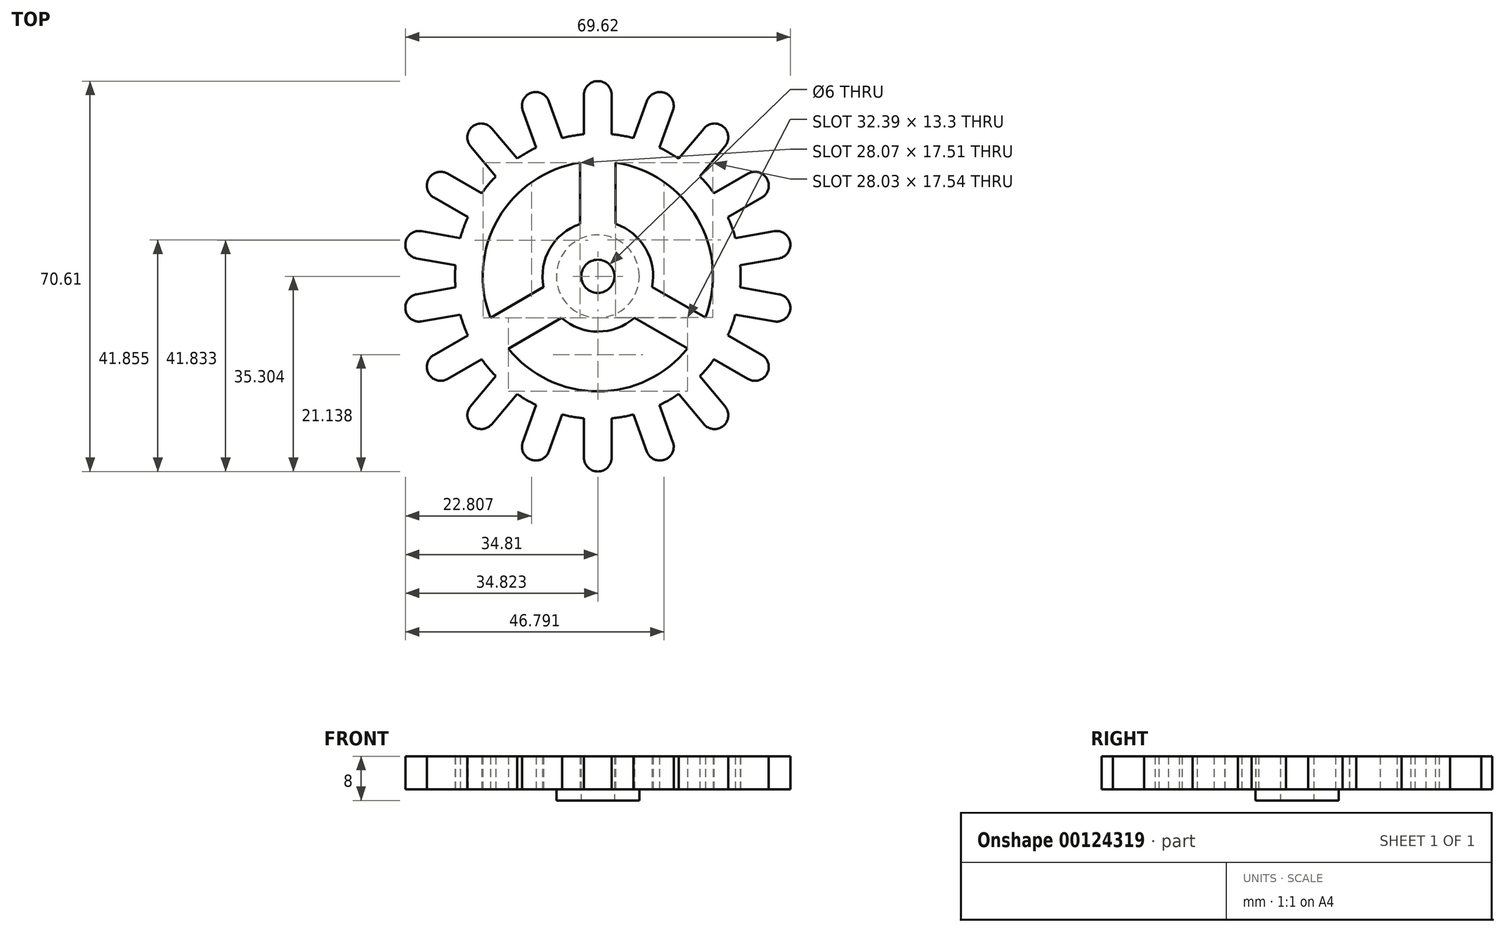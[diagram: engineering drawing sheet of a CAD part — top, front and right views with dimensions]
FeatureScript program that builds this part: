
annotation { "Feature Type Name" : "Feature", "Feature Type Description" : "" }
export const myFeature = defineFeature(function(context is Context, id is Id, definition is map)
    precondition{}
    {
        {
            var Q0;
            Q0=qCreatedBy(makeId("Top.planeOp"),FACE);
            var sketch = newSketch(context, id + "F0", { "sketchPlane" : qUnion([Q0])});
            skLineSegment(sketch, "E0.top", {"start": v(-2.5, 0) * mm, "end": v(2.5, 0) * mm});
            skLineSegment(sketch, "E0.left", {"start": v(-2.5, 7.1) * mm, "end": v(-2.5, 0) * mm});
            skLineSegment(sketch, "E0.right", {"start": v(2.5, 7.1) * mm, "end": v(2.5, 0) * mm});
            skPoint(sketch, "E1.visualSharp", {"position": v(-2.5, 10) * mm});
            skArc(sketch, "E1.filletArc", {"start": v(0, 9.6) * mm, "mid": v(-1.77, 8.88) * mm, "end": v(-2.5, 7.1) * mm});
            skPoint(sketch, "E2.visualSharp", {"position": v(2.5, 10) * mm});
            skArc(sketch, "E2.filletArc", {"start": v(2.5, 7.1) * mm, "mid": v(1.77, 8.88) * mm, "end": v(0, 9.6) * mm});
            skArc(sketch, "E3.1.0", {"start": v(-12.08, 7.48) * mm, "mid": v(-13.49, 6.19) * mm, "end": v(-13.57, 4.28) * mm});
            skArc(sketch, "E3.1.1", {"start": v(-8.87, 5.99) * mm, "mid": v(-10.16, 7.4) * mm, "end": v(-12.08, 7.48) * mm});
            skLineSegment(sketch, "E3.1.2", {"start": v(-8.87, 5.99) * mm, "end": v(-6.44, -0.7) * mm});
            skLineSegment(sketch, "E3.1.3", {"start": v(-11.14, -2.4) * mm, "end": v(-6.44, -0.7) * mm});
            skLineSegment(sketch, "E3.1.4", {"start": v(-13.57, 4.28) * mm, "end": v(-11.14, -2.4) * mm});
            skArc(sketch, "E3.2.0", {"start": v(-22.7, 1.35) * mm, "mid": v(-23.58, -0.35) * mm, "end": v(-23, -2.17) * mm});
            skArc(sketch, "E3.2.1", {"start": v(-19.17, 1.04) * mm, "mid": v(-20.87, 1.93) * mm, "end": v(-22.7, 1.35) * mm});
            skLineSegment(sketch, "E3.2.2", {"start": v(-19.17, 1.04) * mm, "end": v(-14.6, -4.4) * mm});
            skLineSegment(sketch, "E3.2.3", {"start": v(-18.43, -7.62) * mm, "end": v(-14.6, -4.4) * mm});
            skLineSegment(sketch, "E3.2.4", {"start": v(-23, -2.17) * mm, "end": v(-18.43, -7.62) * mm});
            skPoint(sketch, "E3.center", {"position": v(0, -25.7) * mm});
            skArc(sketch, "E4.3.3.0", {"start": v(-30.58, -8.04) * mm, "mid": v(-30.82, -9.94) * mm, "end": v(-29.66, -11.46) * mm});
            skArc(sketch, "E4.4.3.0", {"start": v(-27.16, -7.13) * mm, "mid": v(-29.06, -6.88) * mm, "end": v(-30.58, -8.04) * mm});
            skLineSegment(sketch, "E4.8.3.0", {"start": v(-27.16, -7.13) * mm, "end": v(-21, -10.68) * mm});
            skLineSegment(sketch, "E4.11.3.0", {"start": v(-23.5, -15.01) * mm, "end": v(-21, -10.68) * mm});
            skLineSegment(sketch, "E4.14.3.0", {"start": v(-29.66, -11.46) * mm, "end": v(-23.5, -15.01) * mm});
            skArc(sketch, "E5.3.4.0", {"start": v(-34.77, -19.57) * mm, "mid": v(-34.35, -21.43) * mm, "end": v(-32.74, -22.46) * mm});
            skArc(sketch, "E5.4.4.0", {"start": v(-31.87, -17.54) * mm, "mid": v(-33.74, -17.95) * mm, "end": v(-34.77, -19.57) * mm});
            skLineSegment(sketch, "E5.8.4.0", {"start": v(-31.87, -17.54) * mm, "end": v(-24.87, -18.77) * mm});
            skLineSegment(sketch, "E5.11.4.0", {"start": v(-25.74, -23.7) * mm, "end": v(-24.87, -18.77) * mm});
            skLineSegment(sketch, "E5.14.4.0", {"start": v(-32.74, -22.46) * mm, "end": v(-25.74, -23.7) * mm});
            skArc(sketch, "E6.3.5.0", {"start": v(-34.77, -31.83) * mm, "mid": v(-33.74, -33.44) * mm, "end": v(-31.87, -33.85) * mm});
            skArc(sketch, "E6.4.5.0", {"start": v(-32.74, -28.93) * mm, "mid": v(-34.35, -29.96) * mm, "end": v(-34.77, -31.83) * mm});
            skLineSegment(sketch, "E6.8.5.0", {"start": v(-32.74, -28.93) * mm, "end": v(-25.74, -27.7) * mm});
            skLineSegment(sketch, "E6.11.5.0", {"start": v(-24.87, -32.62) * mm, "end": v(-25.74, -27.7) * mm});
            skLineSegment(sketch, "E6.14.5.0", {"start": v(-31.87, -33.85) * mm, "end": v(-24.87, -32.62) * mm});
            skArc(sketch, "E7.3.6.0", {"start": v(-30.58, -43.35) * mm, "mid": v(-29.06, -44.51) * mm, "end": v(-27.16, -44.26) * mm});
            skArc(sketch, "E7.4.6.0", {"start": v(-29.66, -39.93) * mm, "mid": v(-30.82, -41.45) * mm, "end": v(-30.58, -43.35) * mm});
            skLineSegment(sketch, "E7.8.6.0", {"start": v(-29.66, -39.93) * mm, "end": v(-23.5, -36.38) * mm});
            skLineSegment(sketch, "E7.11.6.0", {"start": v(-21, -40.7) * mm, "end": v(-23.5, -36.38) * mm});
            skLineSegment(sketch, "E7.14.6.0", {"start": v(-27.16, -44.26) * mm, "end": v(-21, -40.7) * mm});
            skArc(sketch, "E8.3.7.0", {"start": v(-22.7, -52.74) * mm, "mid": v(-20.87, -53.32) * mm, "end": v(-19.17, -52.43) * mm});
            skArc(sketch, "E8.4.7.0", {"start": v(-23, -49.22) * mm, "mid": v(-23.58, -51.04) * mm, "end": v(-22.7, -52.74) * mm});
            skLineSegment(sketch, "E8.8.7.0", {"start": v(-23, -49.22) * mm, "end": v(-18.43, -43.77) * mm});
            skLineSegment(sketch, "E8.11.7.0", {"start": v(-14.6, -46.99) * mm, "end": v(-18.43, -43.77) * mm});
            skLineSegment(sketch, "E8.14.7.0", {"start": v(-19.17, -52.43) * mm, "end": v(-14.6, -46.99) * mm});
            skArc(sketch, "E9.3.8.0", {"start": v(-12.08, -58.87) * mm, "mid": v(-10.16, -58.79) * mm, "end": v(-8.87, -57.38) * mm});
            skArc(sketch, "E9.4.8.0", {"start": v(-13.57, -55.67) * mm, "mid": v(-13.49, -57.58) * mm, "end": v(-12.08, -58.87) * mm});
            skLineSegment(sketch, "E9.8.8.0", {"start": v(-13.57, -55.67) * mm, "end": v(-11.14, -48.99) * mm});
            skLineSegment(sketch, "E9.11.8.0", {"start": v(-6.44, -50.7) * mm, "end": v(-11.14, -48.99) * mm});
            skLineSegment(sketch, "E9.14.8.0", {"start": v(-8.87, -57.38) * mm, "end": v(-6.44, -50.7) * mm});
            skArc(sketch, "E10.3.9.0", {"start": v(0, -61) * mm, "mid": v(1.77, -60.27) * mm, "end": v(2.5, -58.5) * mm});
            skArc(sketch, "E10.4.9.0", {"start": v(-2.5, -58.5) * mm, "mid": v(-1.77, -60.27) * mm, "end": v(0, -61) * mm});
            skLineSegment(sketch, "E10.8.9.0", {"start": v(-2.5, -58.5) * mm, "end": v(-2.5, -51.4) * mm});
            skLineSegment(sketch, "E10.11.9.0", {"start": v(2.5, -51.4) * mm, "end": v(-2.5, -51.4) * mm});
            skLineSegment(sketch, "E10.14.9.0", {"start": v(2.5, -58.5) * mm, "end": v(2.5, -51.4) * mm});
            skArc(sketch, "E11.3.10.0", {"start": v(12.08, -58.87) * mm, "mid": v(13.49, -57.58) * mm, "end": v(13.57, -55.67) * mm});
            skArc(sketch, "E11.4.10.0", {"start": v(8.87, -57.38) * mm, "mid": v(10.16, -58.79) * mm, "end": v(12.08, -58.87) * mm});
            skLineSegment(sketch, "E11.8.10.0", {"start": v(8.87, -57.38) * mm, "end": v(6.44, -50.7) * mm});
            skLineSegment(sketch, "E11.11.10.0", {"start": v(11.14, -48.99) * mm, "end": v(6.44, -50.7) * mm});
            skLineSegment(sketch, "E11.14.10.0", {"start": v(13.57, -55.67) * mm, "end": v(11.14, -48.99) * mm});
            skArc(sketch, "E12.3.11.0", {"start": v(22.7, -52.74) * mm, "mid": v(23.58, -51.04) * mm, "end": v(23, -49.22) * mm});
            skArc(sketch, "E12.4.11.0", {"start": v(19.17, -52.43) * mm, "mid": v(20.87, -53.32) * mm, "end": v(22.7, -52.74) * mm});
            skLineSegment(sketch, "E12.8.11.0", {"start": v(19.17, -52.43) * mm, "end": v(14.6, -46.99) * mm});
            skLineSegment(sketch, "E12.11.11.0", {"start": v(18.43, -43.77) * mm, "end": v(14.6, -46.99) * mm});
            skLineSegment(sketch, "E12.14.11.0", {"start": v(23, -49.22) * mm, "end": v(18.43, -43.77) * mm});
            skCircle(sketch, "E13", {"center": v(0, -25.7) * mm, "radius": 25.82 * mm});
            skCircle(sketch, "E14", {"center": v(0, -25.7) * mm, "radius": 20.82 * mm});
            skArc(sketch, "E15.3.12.0", {"start": v(30.58, -43.35) * mm, "mid": v(30.82, -41.45) * mm, "end": v(29.66, -39.93) * mm});
            skArc(sketch, "E15.4.12.0", {"start": v(27.16, -44.26) * mm, "mid": v(29.06, -44.51) * mm, "end": v(30.58, -43.35) * mm});
            skLineSegment(sketch, "E15.8.12.0", {"start": v(27.16, -44.26) * mm, "end": v(21, -40.7) * mm});
            skLineSegment(sketch, "E15.11.12.0", {"start": v(23.5, -36.38) * mm, "end": v(21, -40.7) * mm});
            skLineSegment(sketch, "E15.14.12.0", {"start": v(29.66, -39.93) * mm, "end": v(23.5, -36.38) * mm});
            skArc(sketch, "E15.3.13.0", {"start": v(34.77, -31.83) * mm, "mid": v(34.35, -29.96) * mm, "end": v(32.74, -28.93) * mm});
            skArc(sketch, "E15.4.13.0", {"start": v(31.87, -33.85) * mm, "mid": v(33.74, -33.44) * mm, "end": v(34.77, -31.83) * mm});
            skLineSegment(sketch, "E15.8.13.0", {"start": v(31.87, -33.85) * mm, "end": v(24.87, -32.62) * mm});
            skLineSegment(sketch, "E15.11.13.0", {"start": v(25.74, -27.7) * mm, "end": v(24.87, -32.62) * mm});
            skLineSegment(sketch, "E15.14.13.0", {"start": v(32.74, -28.93) * mm, "end": v(25.74, -27.7) * mm});
            skArc(sketch, "E15.3.14.0", {"start": v(34.77, -19.57) * mm, "mid": v(33.74, -17.95) * mm, "end": v(31.87, -17.54) * mm});
            skArc(sketch, "E15.4.14.0", {"start": v(32.74, -22.46) * mm, "mid": v(34.35, -21.43) * mm, "end": v(34.77, -19.57) * mm});
            skLineSegment(sketch, "E15.8.14.0", {"start": v(32.74, -22.46) * mm, "end": v(25.74, -23.7) * mm});
            skLineSegment(sketch, "E15.11.14.0", {"start": v(24.87, -18.77) * mm, "end": v(25.74, -23.7) * mm});
            skLineSegment(sketch, "E15.14.14.0", {"start": v(31.87, -17.54) * mm, "end": v(24.87, -18.77) * mm});
            skArc(sketch, "E15.3.15.0", {"start": v(30.58, -8.04) * mm, "mid": v(29.06, -6.88) * mm, "end": v(27.16, -7.13) * mm});
            skArc(sketch, "E15.4.15.0", {"start": v(29.66, -11.46) * mm, "mid": v(30.82, -9.94) * mm, "end": v(30.58, -8.04) * mm});
            skLineSegment(sketch, "E15.8.15.0", {"start": v(29.66, -11.46) * mm, "end": v(23.5, -15.01) * mm});
            skLineSegment(sketch, "E15.11.15.0", {"start": v(21, -10.68) * mm, "end": v(23.5, -15.01) * mm});
            skLineSegment(sketch, "E15.14.15.0", {"start": v(27.16, -7.13) * mm, "end": v(21, -10.68) * mm});
            skArc(sketch, "E16.3.16.0", {"start": v(22.7, 1.35) * mm, "mid": v(20.87, 1.93) * mm, "end": v(19.17, 1.04) * mm});
            skArc(sketch, "E16.4.16.0", {"start": v(23, -2.17) * mm, "mid": v(23.58, -0.35) * mm, "end": v(22.7, 1.35) * mm});
            skLineSegment(sketch, "E16.8.16.0", {"start": v(23, -2.17) * mm, "end": v(18.43, -7.62) * mm});
            skLineSegment(sketch, "E16.11.16.0", {"start": v(14.6, -4.4) * mm, "end": v(18.43, -7.62) * mm});
            skLineSegment(sketch, "E16.14.16.0", {"start": v(19.17, 1.04) * mm, "end": v(14.6, -4.4) * mm});
            skArc(sketch, "E16.3.17.0", {"start": v(12.08, 7.48) * mm, "mid": v(10.16, 7.4) * mm, "end": v(8.87, 5.99) * mm});
            skArc(sketch, "E16.4.17.0", {"start": v(13.57, 4.28) * mm, "mid": v(13.49, 6.19) * mm, "end": v(12.08, 7.48) * mm});
            skLineSegment(sketch, "E16.8.17.0", {"start": v(13.57, 4.28) * mm, "end": v(11.14, -2.4) * mm});
            skLineSegment(sketch, "E16.11.17.0", {"start": v(6.44, -0.7) * mm, "end": v(11.14, -2.4) * mm});
            skLineSegment(sketch, "E16.14.17.0", {"start": v(8.87, 5.99) * mm, "end": v(6.44, -0.7) * mm});
            skCircle(sketch, "E17", {"center": v(0, -25.7) * mm, "radius": 10 * mm});
            skCircle(sketch, "E18", {"center": v(0, -25.7) * mm, "radius": 3 * mm});
            skCircle(sketch, "E19", {"center": v(0, -25.7) * mm, "radius": 7.5 * mm});
            skLineSegment(sketch, "E20.left", {"start": v(-3.25, -5.13) * mm, "end": v(-3.25, -16.24) * mm});
            skLineSegment(sketch, "E20.right", {"start": v(3.2, -5.13) * mm, "end": v(3.2, -16.22) * mm});
            skPoint(sketch, "E21", {"position": v(0, -4.88) * mm});
            skLineSegment(sketch, "E22.1.0", {"start": v(-16.18, -38.8) * mm, "end": v(-6.56, -33.24) * mm});
            skLineSegment(sketch, "E22.1.1", {"start": v(-19.42, -33.2) * mm, "end": v(-9.8, -27.65) * mm});
            skLineSegment(sketch, "E22.2.0", {"start": v(19.43, -33.16) * mm, "end": v(9.82, -27.6) * mm});
            skLineSegment(sketch, "E22.2.1", {"start": v(16.2, -38.76) * mm, "end": v(6.6, -33.21) * mm});
            skPoint(sketch, "E23", {"position": v(0, 9.6) * mm});
            skSolve(sketch);
        }
        {
            var Q0;
            {var subQ0=sQuery(id+"F0.wireOp",EDGE,"E6.11.5.0");Q0=makeQuery(id+"F0.imprint","IMPRINT",FACE,{"disambiguationData":[TD([[makeQuery(id+"F0.imprint","IMPRINT",EDGE,{"derivedFrom":subQ0}),1.0]])]});}
            var Q1;
            {var subQ0=sQuery(id+"F0.wireOp",EDGE,"E22.1.0");Q1=makeQuery(id+"F0.imprint","IMPRINT",FACE,{"disambiguationData":[TD([[makeQuery(id+"F0.imprint","IMPRINT",EDGE,{"derivedFrom":subQ0}),1.0]])]});}
            var Q2;
            Q2=makeQuery(id+"F0.imprint","IMPRINT",FACE,{"disambiguationData":[TD([[makeQuery(id+"F0.imprint","IMPRINT",EDGE,{"derivedFrom":sQuery(id+"F0.wireOp",EDGE,"E15.3.14.0")}),1.0]])]});
            var Q3;
            Q3=makeQuery(id+"F0.imprint","IMPRINT",FACE,{"disambiguationData":[TD([[makeQuery(id+"F0.imprint","IMPRINT",EDGE,{"derivedFrom":sQuery(id+"F0.wireOp",EDGE,"E12.3.11.0")}),1.0]])]});
            var Q4;
            Q4=makeQuery(id+"F0.imprint","IMPRINT",FACE,{"disambiguationData":[TD([[makeQuery(id+"F0.imprint","IMPRINT",EDGE,{"derivedFrom":sQuery(id+"F0.wireOp",EDGE,"E11.3.10.0")}),1.0]])]});
            var Q5;
            Q5=makeQuery(id+"F0.imprint","IMPRINT",FACE,{"disambiguationData":[TD([[makeQuery(id+"F0.imprint","IMPRINT",EDGE,{"derivedFrom":sQuery(id+"F0.wireOp",EDGE,"E10.3.9.0")}),1.0]])]});
            var Q6;
            Q6=makeQuery(id+"F0.imprint","IMPRINT",FACE,{"disambiguationData":[TD([[makeQuery(id+"F0.imprint","IMPRINT",EDGE,{"derivedFrom":sQuery(id+"F0.wireOp",EDGE,"E9.3.8.0")}),1.0]])]});
            var Q7;
            Q7=makeQuery(id+"F0.imprint","IMPRINT",FACE,{"disambiguationData":[TD([[makeQuery(id+"F0.imprint","IMPRINT",EDGE,{"derivedFrom":sQuery(id+"F0.wireOp",EDGE,"E8.3.7.0")}),1.0]])]});
            var Q8;
            Q8=makeQuery(id+"F0.imprint","IMPRINT",FACE,{"disambiguationData":[TD([[makeQuery(id+"F0.imprint","IMPRINT",EDGE,{"derivedFrom":sQuery(id+"F0.wireOp",EDGE,"E7.3.6.0")}),1.0]])]});
            var Q9;
            Q9=makeQuery(id+"F0.imprint","IMPRINT",FACE,{"disambiguationData":[TD([[makeQuery(id+"F0.imprint","IMPRINT",EDGE,{"derivedFrom":sQuery(id+"F0.wireOp",EDGE,"E6.3.5.0")}),1.0]])]});
            var Q10;
            Q10=makeQuery(id+"F0.imprint","IMPRINT",FACE,{"disambiguationData":[TD([[makeQuery(id+"F0.imprint","IMPRINT",EDGE,{"derivedFrom":sQuery(id+"F0.wireOp",EDGE,"E5.3.4.0")}),1.0]])]});
            var Q11;
            Q11=makeQuery(id+"F0.imprint","IMPRINT",FACE,{"disambiguationData":[TD([[makeQuery(id+"F0.imprint","IMPRINT",EDGE,{"derivedFrom":sQuery(id+"F0.wireOp",EDGE,"E4.3.3.0")}),1.0]])]});
            var Q12;
            Q12=makeQuery(id+"F0.imprint","IMPRINT",FACE,{"disambiguationData":[TD([[makeQuery(id+"F0.imprint","IMPRINT",EDGE,{"derivedFrom":sQuery(id+"F0.wireOp",EDGE,"E3.2.0")}),1.0]])]});
            var Q13;
            Q13=makeQuery(id+"F0.imprint","IMPRINT",FACE,{"disambiguationData":[TD([[makeQuery(id+"F0.imprint","IMPRINT",EDGE,{"derivedFrom":sQuery(id+"F0.wireOp",EDGE,"E3.1.0")}),1.0]])]});
            var Q14;
            {var subQ1=sQuery(id+"F0.wireOp",EDGE,"E0.left");Q14=makeQuery(id+"F0.imprint","IMPRINT",FACE,{"disambiguationData":[TD([[makeQuery(id+"F0.imprint","IMPRINT",EDGE,{"derivedFrom":subQ1}),1.0]])]});}
            var Q15;
            Q15=makeQuery(id+"F0.imprint","IMPRINT",FACE,{"disambiguationData":[TD([[makeQuery(id+"F0.imprint","IMPRINT",EDGE,{"derivedFrom":sQuery(id+"F0.wireOp",EDGE,"E16.3.16.0")}),1.0]])]});
            var Q16;
            Q16=makeQuery(id+"F0.imprint","IMPRINT",FACE,{"disambiguationData":[TD([[makeQuery(id+"F0.imprint","IMPRINT",EDGE,{"derivedFrom":sQuery(id+"F0.wireOp",EDGE,"E15.3.15.0")}),1.0]])]});
            var Q17;
            Q17=makeQuery(id+"F0.imprint","IMPRINT",FACE,{"disambiguationData":[TD([[makeQuery(id+"F0.imprint","IMPRINT",EDGE,{"derivedFrom":sQuery(id+"F0.wireOp",EDGE,"E16.3.17.0")}),1.0]])]});
            var Q18;
            {var subQ0=sQuery(id+"F0.wireOp",EDGE,"E4.11.3.0");Q18=makeQuery(id+"F0.imprint","IMPRINT",FACE,{"disambiguationData":[TD([[makeQuery(id+"F0.imprint","IMPRINT",EDGE,{"derivedFrom":subQ0}),1.0]])]});}
            var Q19;
            {var subQ0=sQuery(id+"F0.wireOp",EDGE,"E20.left");Q19=makeQuery(id+"F0.imprint","IMPRINT",FACE,{"disambiguationData":[TD([[makeQuery(id+"F0.imprint","IMPRINT",EDGE,{"derivedFrom":subQ0}),1.0]])]});}
            var Q20;
            Q20=makeQuery(id+"F0.imprint","IMPRINT",FACE,{"disambiguationData":[TD([[makeQuery(id+"F0.imprint","IMPRINT",EDGE,{"derivedFrom":sQuery(id+"F0.wireOp",EDGE,"E18")}),-1.0]])]});
            var Q21;
            Q21=makeQuery(id+"F0.imprint","IMPRINT",FACE,{"disambiguationData":[TD([[makeQuery(id+"F0.imprint","IMPRINT",EDGE,{"derivedFrom":sQuery(id+"F0.wireOp",EDGE,"E15.3.13.0")}),1.0]])]});
            var Q22;
            Q22=makeQuery(id+"F0.imprint","IMPRINT",FACE,{"disambiguationData":[TD([[makeQuery(id+"F0.imprint","IMPRINT",EDGE,{"derivedFrom":sQuery(id+"F0.wireOp",EDGE,"E15.3.12.0")}),1.0]])]});
            var Q23;
            Q23=makeQuery(id+"F0.imprint","IMPRINT",FACE,{"disambiguationData":[TD([[makeQuery(id+"F0.imprint","IMPRINT",EDGE,{"derivedFrom":sQuery(id+"F0.wireOp",EDGE,"E19")}),-1.0]])]});
            var Q24;
            {var subQ0=sQuery(id+"F0.wireOp",EDGE,"E9.11.8.0");Q24=makeQuery(id+"F0.imprint","IMPRINT",FACE,{"disambiguationData":[TD([[makeQuery(id+"F0.imprint","IMPRINT",EDGE,{"derivedFrom":subQ0}),1.0]])]});}
            var Q25;
            {var subQ5=sQuery(id+"F0.wireOp",EDGE,"E0.top");Q25=makeQuery(id+"F0.imprint","IMPRINT",FACE,{"disambiguationData":[TD([[makeQuery(id+"F0.imprint","IMPRINT",EDGE,{"derivedFrom":subQ5}),-1.0]])]});}
            var Q26;
            {var subQ0=sQuery(id+"F0.wireOp",EDGE,"E22.2.0");Q26=makeQuery(id+"F0.imprint","IMPRINT",FACE,{"disambiguationData":[TD([[makeQuery(id+"F0.imprint","IMPRINT",EDGE,{"derivedFrom":subQ0}),1.0]])]});}
            var Q27;
            {var subQ0=sQuery(id+"F0.wireOp",EDGE,"E3.2.3");Q27=makeQuery(id+"F0.imprint","IMPRINT",FACE,{"disambiguationData":[TD([[makeQuery(id+"F0.imprint","IMPRINT",EDGE,{"derivedFrom":subQ0}),1.0]])]});}
            var Q28;
            {var subQ0=sQuery(id+"F0.wireOp",EDGE,"E15.11.13.0");Q28=makeQuery(id+"F0.imprint","IMPRINT",FACE,{"disambiguationData":[TD([[makeQuery(id+"F0.imprint","IMPRINT",EDGE,{"derivedFrom":subQ0}),1.0]])]});}
            var Q29;
            {var subQ0=sQuery(id+"F0.wireOp",EDGE,"E3.1.3");Q29=makeQuery(id+"F0.imprint","IMPRINT",FACE,{"disambiguationData":[TD([[makeQuery(id+"F0.imprint","IMPRINT",EDGE,{"derivedFrom":subQ0}),1.0]])]});}
            var Q30;
            {var subQ0=sQuery(id+"F0.wireOp",EDGE,"E15.11.12.0");Q30=makeQuery(id+"F0.imprint","IMPRINT",FACE,{"disambiguationData":[TD([[makeQuery(id+"F0.imprint","IMPRINT",EDGE,{"derivedFrom":subQ0}),1.0]])]});}
            var Q31;
            {var subQ0=sQuery(id+"F0.wireOp",EDGE,"E0.top");Q31=makeQuery(id+"F0.imprint","IMPRINT",FACE,{"disambiguationData":[TD([[makeQuery(id+"F0.imprint","IMPRINT",EDGE,{"derivedFrom":subQ0}),1.0]])]});}
            var Q32;
            {var subQ0=sQuery(id+"F0.wireOp",EDGE,"E16.11.17.0");Q32=makeQuery(id+"F0.imprint","IMPRINT",FACE,{"disambiguationData":[TD([[makeQuery(id+"F0.imprint","IMPRINT",EDGE,{"derivedFrom":subQ0}),1.0]])]});}
            var Q33;
            {var subQ0=sQuery(id+"F0.wireOp",EDGE,"E16.11.16.0");Q33=makeQuery(id+"F0.imprint","IMPRINT",FACE,{"disambiguationData":[TD([[makeQuery(id+"F0.imprint","IMPRINT",EDGE,{"derivedFrom":subQ0}),1.0]])]});}
            var Q34;
            {var subQ0=sQuery(id+"F0.wireOp",EDGE,"E15.11.15.0");Q34=makeQuery(id+"F0.imprint","IMPRINT",FACE,{"disambiguationData":[TD([[makeQuery(id+"F0.imprint","IMPRINT",EDGE,{"derivedFrom":subQ0}),1.0]])]});}
            var Q35;
            {var subQ0=sQuery(id+"F0.wireOp",EDGE,"E7.11.6.0");Q35=makeQuery(id+"F0.imprint","IMPRINT",FACE,{"disambiguationData":[TD([[makeQuery(id+"F0.imprint","IMPRINT",EDGE,{"derivedFrom":subQ0}),1.0]])]});}
            var Q36;
            {var subQ0=sQuery(id+"F0.wireOp",EDGE,"E10.11.9.0");Q36=makeQuery(id+"F0.imprint","IMPRINT",FACE,{"disambiguationData":[TD([[makeQuery(id+"F0.imprint","IMPRINT",EDGE,{"derivedFrom":subQ0}),1.0]])]});}
            var Q37;
            {var subQ0=sQuery(id+"F0.wireOp",EDGE,"E15.11.14.0");Q37=makeQuery(id+"F0.imprint","IMPRINT",FACE,{"disambiguationData":[TD([[makeQuery(id+"F0.imprint","IMPRINT",EDGE,{"derivedFrom":subQ0}),1.0]])]});}
            var Q38;
            {var subQ0=sQuery(id+"F0.wireOp",EDGE,"E11.11.10.0");Q38=makeQuery(id+"F0.imprint","IMPRINT",FACE,{"disambiguationData":[TD([[makeQuery(id+"F0.imprint","IMPRINT",EDGE,{"derivedFrom":subQ0}),1.0]])]});}
            var Q39;
            {var subQ0=sQuery(id+"F0.wireOp",EDGE,"E8.11.7.0");Q39=makeQuery(id+"F0.imprint","IMPRINT",FACE,{"disambiguationData":[TD([[makeQuery(id+"F0.imprint","IMPRINT",EDGE,{"derivedFrom":subQ0}),1.0]])]});}
            var Q40;
            {var subQ0=sQuery(id+"F0.wireOp",EDGE,"E5.11.4.0");Q40=makeQuery(id+"F0.imprint","IMPRINT",FACE,{"disambiguationData":[TD([[makeQuery(id+"F0.imprint","IMPRINT",EDGE,{"derivedFrom":subQ0}),1.0]])]});}
            var Q41;
            {var subQ0=sQuery(id+"F0.wireOp",EDGE,"E12.11.11.0");Q41=makeQuery(id+"F0.imprint","IMPRINT",FACE,{"disambiguationData":[TD([[makeQuery(id+"F0.imprint","IMPRINT",EDGE,{"derivedFrom":subQ0}),1.0]])]});}
            extrude(context, id + "F1", {"entities" : qUnion([Q0, Q1, Q2, Q3, Q4, Q5, Q6, Q7, Q8, Q9, Q10, Q11, Q12, Q13, Q14, Q15, Q16, Q17, Q18, Q19, Q20, Q21, Q22, Q23, Q24, Q25, Q26, Q27, Q28, Q29, Q30, Q31, Q32, Q33, Q34, Q35, Q36, Q37, Q38, Q39, Q40, Q41]), "depth" : 6 * mm});
        }
        {
            var Q0;
            Q0=makeQuery(id+"F0.imprint","IMPRINT",FACE,{"disambiguationData":[TD([[makeQuery(id+"F0.imprint","IMPRINT",EDGE,{"derivedFrom":sQuery(id+"F0.wireOp",EDGE,"E18")}),-1.0]])]});
            extrude(context, id + "F2", {"entities" : qUnion([Q0]), "operationType" : NewBodyOperationType.ADD, "oppositeDirection" : true, "depth" : 2 * mm});
        }
    });
